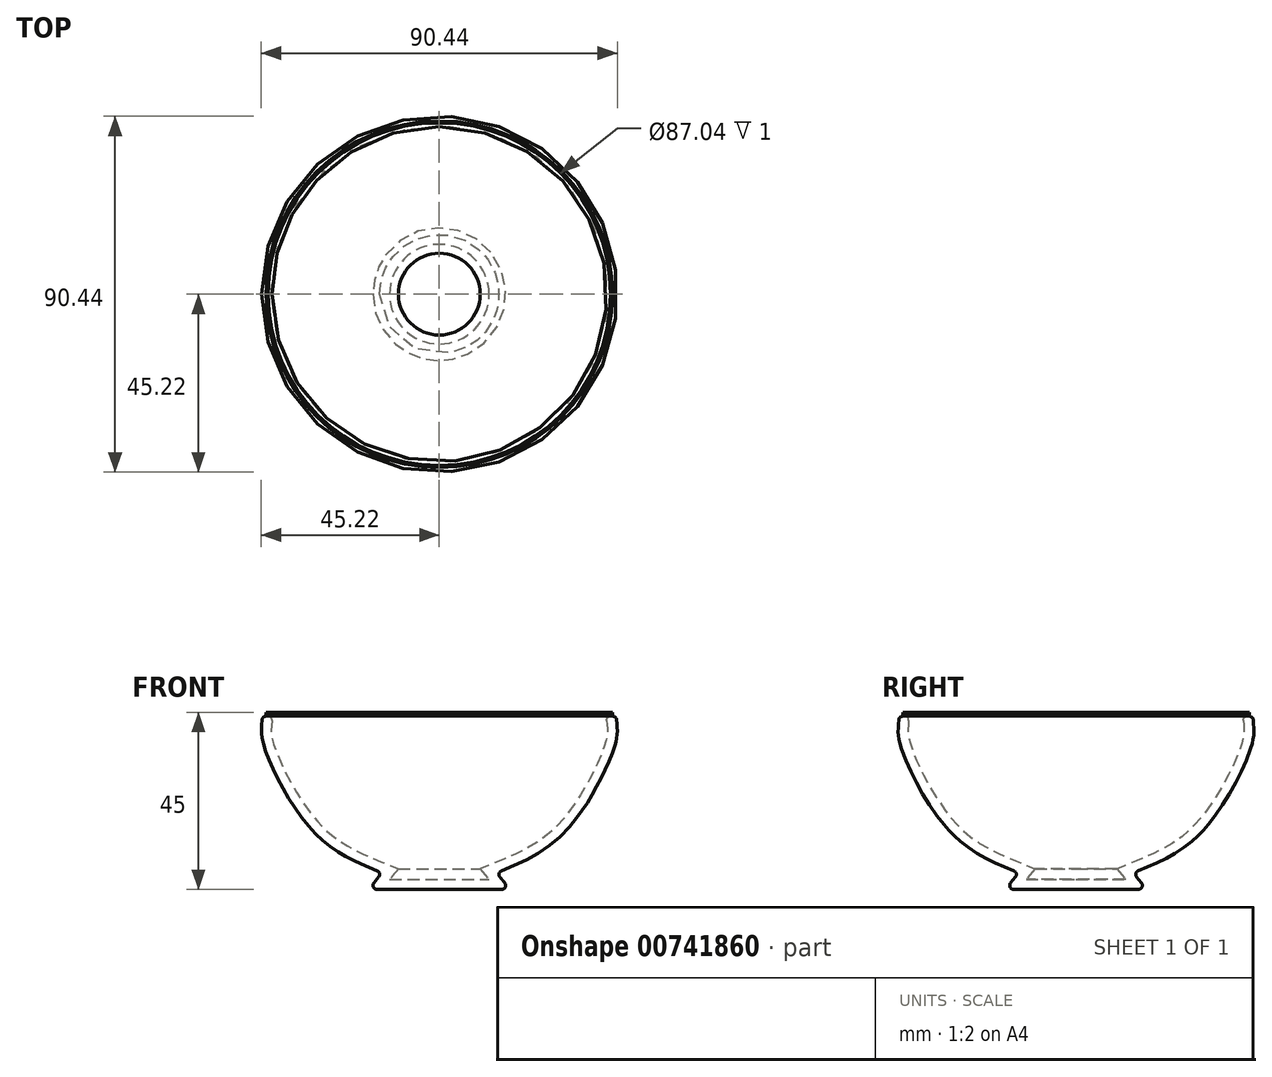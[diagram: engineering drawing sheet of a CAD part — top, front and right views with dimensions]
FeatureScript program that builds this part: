
annotation { "Feature Type Name" : "Feature", "Feature Type Description" : "" }
export const myFeature = defineFeature(function(context is Context, id is Id, definition is map)
    precondition{}
    {
        {
            var Q0;
            Q0=qCreatedBy(makeId("Front.planeOp"),FACE);
            var sketch = newSketch(context, id + "F0", { "sketchPlane" : qUnion([Q0])});
            skLineSegment(sketch, "E0", {"start": v(0, 0) * mm, "end": v(18, 0) * mm});
            skLineSegment(sketch, "E1", {"start": v(0, 0) * mm, "end": v(0, 44) * mm});
            skLineSegment(sketch, "E2", {"start": v(0, 44) * mm, "end": v(45, 44) * mm});
            skLineSegment(sketch, "E3", {"start": v(18, 0) * mm, "end": v(14.5, 4.17) * mm});
            skFitSpline(sketch, "E4", {"points": [v(45, 44) * mm, v(45, 38.12) * mm, v(32.46, 15.17) * mm, v(14.5, 4.17) * mm], "startDerivative": vector(0, -39.9) * mm, "endDerivative": vector(-49.44, -20.28) * mm});
            skSolve(sketch);
        }
        {
            var Q0;
            Q0=makeQuery(id+"F0.imprint","IMPRINT",FACE,{"disambiguationData":[TD([[makeQuery(id+"F0.imprint","IMPRINT",EDGE,{"derivedFrom":sQuery(id+"F0.wireOp",EDGE,"E0")}),1.0]])]});
            var Q1;
            Q1=sQuery(id+"F0.wireOp",EDGE,"E1");
            revolve(context, id + "F1", {"surfaceOperationType" : NewSurfaceOperationType.NEW, "entities" : qUnion([Q0]), "axis" : qUnion([Q1]), "revolveType" : RevolveType.FULL});
        }
        {
            var Q0;
            Q0=makeQuery(id+"F1.opRevolve","SWEPT_FACE",FACE,{"disambiguationData":[OSD([sQuery(id+"F0.wireOp",EDGE,"E2")])]});
            var sketch = newSketch(context, id + "F2", { "sketchPlane" : qUnion([Q0])});
            skArc(sketch, "E5", {"start": v(-56.49, 0) * mm, "mid": v(-55.2, 4.04) * mm, "end": v(-51.83, 6.6) * mm});
            skLineSegment(sketch, "E6", {"start": v(-51.83, 6.6) * mm, "end": v(0, 25) * mm});
            skLineSegment(sketch, "E7", {"start": v(0, 25) * mm, "end": v(0, 0) * mm});
            skArc(sketch, "E8.MirrorCS", {"start": v(-56.49, 0) * mm, "mid": v(-55.2, -4.04) * mm, "end": v(-51.83, -6.6) * mm});
            skLineSegment(sketch, "E9.MirrorCS", {"start": v(-51.83, -6.6) * mm, "end": v(0, -25) * mm});
            skLineSegment(sketch, "E10.MirrorCS", {"start": v(0, -25) * mm, "end": v(0, 0) * mm});
            skSolve(sketch);
        }
        {
            var Q0;
            Q0=qCreatedBy(makeId("Front.planeOp"),FACE);
            var sketch = newSketch(context, id + "F3", { "sketchPlane" : qUnion([Q0])});
            skLineSegment(sketch, "E11", {"start": v(0, 44) * mm, "end": v(28.98, 36.24) * mm});
            skSolve(sketch);
        }
        {
            var Q0;
            {var subQ7=sQuery(id+"F2.wireOp",EDGE,"E5");Q0=makeQuery(id+"F2.imprint","IMPRINT",FACE,{"disambiguationData":[TD([[makeQuery(id+"F2.imprint","IMPRINT",EDGE,{"derivedFrom":subQ7}),-1.0]])]});}
            var Q1;
            {var subQ1=sQuery(id+"F2.wireOp",EDGE,"E7");Q1=makeQuery(id+"F2.imprint","IMPRINT",FACE,{"disambiguationData":[TD([[makeQuery(id+"F2.imprint","IMPRINT",EDGE,{"derivedFrom":subQ1}),-1.0]])]});}
            var Q2;
            Q2=sQuery(id+"F3.wireOp",EDGE,"E11");
            sweep(context, id + "F4", {"operationType" : NewBodyOperationType.ADD, "profiles" : qUnion([Q0, Q1]), "path" : qUnion([Q2])});
        }
        {
            var Q0;
            Q0=makeQuery(id+"F1.opRevolve","SWEPT_FACE",FACE,{"disambiguationData":[OSD([sQuery(id+"F0.wireOp",EDGE,"E2")])]});
            shell(context, id + "F5", {"entities" : qUnion([Q0]), "thickness" : 2.5 * mm});
        }
        {
            var Q0;
            Q0=makeQuery(id+"F1.opRevolve","SWEPT_FACE",FACE,{"disambiguationData":[OSD([sQuery(id+"F0.wireOp",EDGE,"E3")])]});
            var Q1;
            Q1=makeQuery(id+"F1.opRevolve","SWEPT_EDGE",EDGE,{"disambiguationData":[OSD([sQuery(id+"F0.wireOp",EDGE,"E2"),sQuery(id+"F0.wireOp",EDGE,"E4")])]});
            var Q2;
            Q2=makeQuery(id+"F5.opShell","OFFSET_EDGE",EDGE,{"disambiguationData":[OSD([sQuery(id+"F0.wireOp",EDGE,"E2"),sQuery(id+"F0.wireOp",EDGE,"E4")])]});
            fillet(context, id + "F6", {"entities" : qUnion([Q0, Q1, Q2]), "radius" : 1 * mm, "tangentPropagation" : true, "allowEdgeOverflow" : false});
        }
        {
            var Q0;
            Q0=makeQuery(id+"F1.opRevolve","SWEPT_FACE",FACE,{"disambiguationData":[OSD([sQuery(id+"F0.wireOp",EDGE,"E2")])]});
            extrude(context, id + "F7", {"entities" : qUnion([Q0]), "operationType" : NewBodyOperationType.ADD, "depth" : 1 * mm, "offsetDistance" : 25 * mm});
        }
    });
